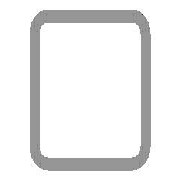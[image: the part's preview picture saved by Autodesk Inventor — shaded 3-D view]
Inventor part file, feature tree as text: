
AUTODESK INVENTOR PART (.ipt)
format: ipt  version: 2025.3 (Build 293356030, 356C)  size: 150,016 bytes
history: native  units: mm (DEFAULTED — no unit token found)
features: other x4, plane x3, split x2, sketch x1
ambient origin geometry x8: Origin, YZ Plane, XZ Plane, XY Plane, X Axis, Y Axis, Z Axis, Center Point
bodies: Solid1 (feature_tree), Body (feature_tree)
feature tree (10):
  parser-record x1  (decoder bookkeeping rows leaked as tree rows — omitted from the tree; the rows remain in map.json)
  other  "Driven Length"
  other  "Start Plane"
  other  "End Plane"
  plane  "Work Plane4"
  split  "Split1"
  plane  "Work Plane5"
  split  "Split2"
  sketch  "Sketch3"  dims[d3=3205.095951mm d4=0.0mm d7=6.0mm d9=60.0mm d11=60.0mm d12=3.0mm d13=81.652089mm d14=3286.748039mm d15=30.0mm d16=30.0mm d17=90.0deg d18=3205.095951mm]
  plane  "Work Plane3"
